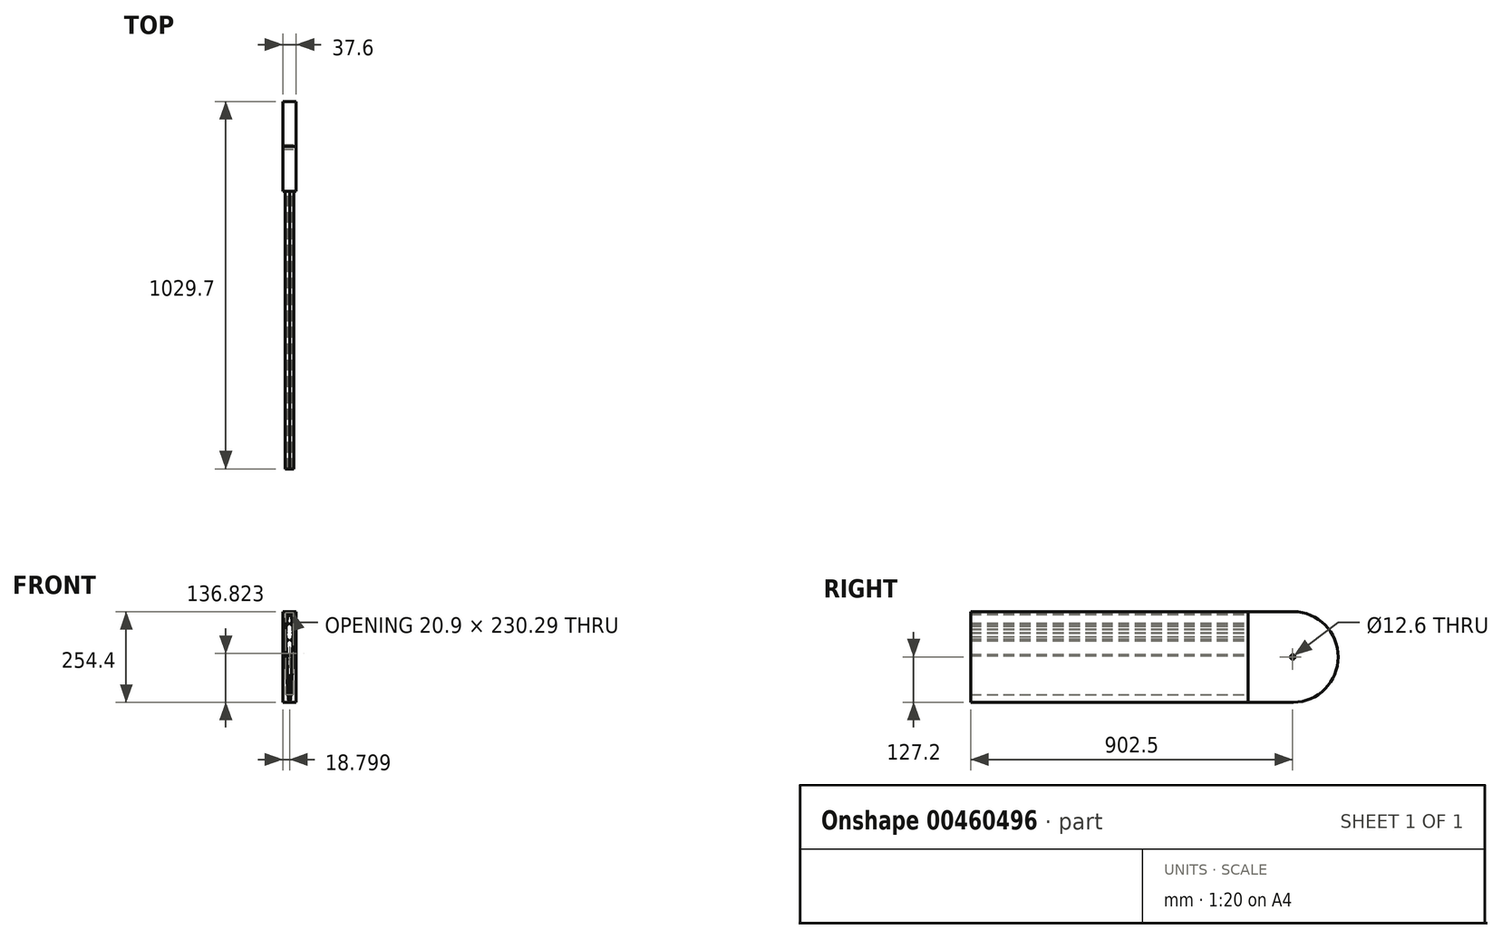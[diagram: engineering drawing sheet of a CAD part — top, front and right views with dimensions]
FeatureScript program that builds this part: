
annotation { "Feature Type Name" : "Feature", "Feature Type Description" : "" }
export const myFeature = defineFeature(function(context is Context, id is Id, definition is map)
    precondition{}
    {
        {
            var Q0;
            Q0=qCreatedBy(makeId("Front.planeOp"),FACE);
            var sketch = newSketch(context, id + "F0", { "sketchPlane" : qUnion([Q0])});
            skLineSegment(sketch, "E0", {"start": v(-26, 84.74) * mm, "end": v(-24.5, 84.74) * mm});
            skArc(sketch, "E1", {"start": v(-26.25, 85) * mm, "mid": v(-26.17, 84.82) * mm, "end": v(-26, 84.74) * mm});
            skFitSpline(sketch, "E2", {"points": [v(-26.25, 85) * mm, v(-26.24, 88.67) * mm, v(-26.08, 98.58) * mm, v(-25.1, 113) * mm, v(-22.87, 125.21) * mm, v(-20.9, 130.42) * mm, v(-19.33, 133.17) * mm, v(-17.9, 134.65) * mm, v(-16.79, 135) * mm, v(-16.24, 135) * mm]});
            skFitSpline(sketch, "E3", {"points": [v(-16.24, 135) * mm, v(-15.7, 135) * mm, v(-14.58, 134.65) * mm, v(-13.16, 133.17) * mm, v(-11.58, 130.42) * mm, v(-9.61, 125.21) * mm, v(-7.38, 113) * mm, v(-6.4, 98.58) * mm, v(-6.24, 88.67) * mm, v(-6.24, 85) * mm]});
            skArc(sketch, "E4", {"start": v(-6.49, 84.74) * mm, "mid": v(-6.3, 84.82) * mm, "end": v(-6.24, 85) * mm});
            skLineSegment(sketch, "E5", {"start": v(-7.99, 84.74) * mm, "end": v(-6.49, 84.74) * mm});
            skArc(sketch, "E6", {"start": v(-7.99, 84.74) * mm, "mid": v(-8.16, 84.67) * mm, "end": v(-8.24, 84.5) * mm});
            skLineSegment(sketch, "E7", {"start": v(-8.24, 84.5) * mm, "end": v(-8.24, 75) * mm});
            skArc(sketch, "E8", {"start": v(-10.24, 88.79) * mm, "mid": v(-10.27, 88.98) * mm, "end": v(-10.38, 89.14) * mm});
            skLineSegment(sketch, "E9", {"start": v(-11.41, 90.17) * mm, "end": v(-10.38, 89.14) * mm});
            skArc(sketch, "E10", {"start": v(-11.44, 90.85) * mm, "mid": v(-11.56, 90.5) * mm, "end": v(-11.41, 90.17) * mm});
            skArc(sketch, "E11", {"start": v(-11.44, 90.85) * mm, "mid": v(-9.9, 95) * mm, "end": v(-11.44, 99.15) * mm});
            skArc(sketch, "E12", {"start": v(-11.41, 99.83) * mm, "mid": v(-11.56, 99.5) * mm, "end": v(-11.44, 99.15) * mm});
            skLineSegment(sketch, "E13", {"start": v(-11.41, 99.83) * mm, "end": v(-9.68, 101.56) * mm});
            skArc(sketch, "E14", {"start": v(-9.68, 101.56) * mm, "mid": v(-9, 102.63) * mm, "end": v(-8.81, 103.89) * mm});
            skFitSpline(sketch, "E15", {"points": [v(-8.81, 103.89) * mm, v(-8.97, 106.15) * mm, v(-9.72, 114.71) * mm, v(-11.32, 123.38) * mm, v(-12.63, 127.4) * mm, v(-12.98, 128.32) * mm]});
            skArc(sketch, "E16", {"start": v(-12.98, 128.32) * mm, "mid": v(-13.34, 128.63) * mm, "end": v(-13.8, 128.5) * mm});
            skArc(sketch, "E17", {"start": v(-14.5, 127.97) * mm, "mid": v(-14.13, 128.21) * mm, "end": v(-13.8, 128.5) * mm});
            skArc(sketch, "E18", {"start": v(-15.24, 128.4) * mm, "mid": v(-15, 127.97) * mm, "end": v(-14.5, 127.97) * mm});
            skLineSegment(sketch, "E19", {"start": v(-15.24, 129) * mm, "end": v(-15.24, 128.4) * mm});
            skArc(sketch, "E20", {"start": v(-15.04, 129.4) * mm, "mid": v(-15.19, 129.22) * mm, "end": v(-15.24, 129) * mm});
            skArc(sketch, "E21", {"start": v(-15.04, 129.4) * mm, "mid": v(-16.24, 133) * mm, "end": v(-17.44, 129.4) * mm});
            skArc(sketch, "E22", {"start": v(-17.24, 129) * mm, "mid": v(-17.3, 129.22) * mm, "end": v(-17.44, 129.4) * mm});
            skLineSegment(sketch, "E23", {"start": v(-17.24, 128.4) * mm, "end": v(-17.24, 129) * mm});
            skArc(sketch, "E24", {"start": v(-18, 127.97) * mm, "mid": v(-17.5, 127.97) * mm, "end": v(-17.24, 128.4) * mm});
            skArc(sketch, "E25", {"start": v(-18.69, 128.5) * mm, "mid": v(-18.36, 128.21) * mm, "end": v(-18, 127.97) * mm});
            skArc(sketch, "E26", {"start": v(-18.69, 128.5) * mm, "mid": v(-19.15, 128.63) * mm, "end": v(-19.5, 128.32) * mm});
            skFitSpline(sketch, "E27", {"points": [v(-19.5, 128.32) * mm, v(-19.86, 127.4) * mm, v(-21.16, 123.38) * mm, v(-22.76, 114.71) * mm, v(-23.52, 106.15) * mm, v(-23.67, 103.89) * mm]});
            skArc(sketch, "E28", {"start": v(-23.67, 103.89) * mm, "mid": v(-23.49, 102.63) * mm, "end": v(-22.8, 101.56) * mm});
            skLineSegment(sketch, "E29", {"start": v(-22.8, 101.56) * mm, "end": v(-21.07, 99.83) * mm});
            skArc(sketch, "E30", {"start": v(-21.05, 99.15) * mm, "mid": v(-20.93, 99.5) * mm, "end": v(-21.07, 99.83) * mm});
            skArc(sketch, "E31", {"start": v(-21.05, 99.15) * mm, "mid": v(-22.6, 95) * mm, "end": v(-21.05, 90.85) * mm});
            skArc(sketch, "E32", {"start": v(-21.07, 90.17) * mm, "mid": v(-20.93, 90.5) * mm, "end": v(-21.05, 90.85) * mm});
            skLineSegment(sketch, "E33", {"start": v(-22.1, 89.14) * mm, "end": v(-21.07, 90.17) * mm});
            skArc(sketch, "E34", {"start": v(-22.1, 89.14) * mm, "mid": v(-22.2, 88.98) * mm, "end": v(-22.25, 88.79) * mm});
            skLineSegment(sketch, "E35", {"start": v(-24.25, 75) * mm, "end": v(-24.25, 84.5) * mm});
            skArc(sketch, "E36", {"start": v(-24.25, 84.5) * mm, "mid": v(-24.32, 84.67) * mm, "end": v(-24.5, 84.74) * mm});
            skLineSegment(sketch, "E37", {"start": v(-8.24, 75) * mm, "end": v(-10.24, 75) * mm});
            skLineSegment(sketch, "E38", {"start": v(-22.25, 88.79) * mm, "end": v(-22.25, 75) * mm});
            skLineSegment(sketch, "E39", {"start": v(-22.25, 75) * mm, "end": v(-24.25, 75) * mm});
            skLineSegment(sketch, "E40", {"start": v(-10.24, 75) * mm, "end": v(-10.24, 88.79) * mm});
            skArc(sketch, "E41", {"start": v(1.9, 35) * mm, "mid": v(5.19, -30.83) * mm, "end": v(9.73, -96.58) * mm});
            skFitSpline(sketch, "E42", {"points": [v(1.9, 35) * mm, v(1.67, 41.44) * mm, v(1.23, 54.34) * mm, v(1.24, 72.62) * mm, v(1.85, 89.82) * mm, v(2.95, 103.2) * mm, v(4.43, 113.85) * mm, v(5.71, 120.45) * mm, v(7.11, 125.63) * mm, v(8.23, 128.8) * mm, v(9.37, 131.23) * mm, v(10.3, 132.77) * mm, v(11.33, 133.95) * mm, v(12.42, 134.8) * mm, v(13.31, 134.93) * mm, v(13.76, 135) * mm]});
            skFitSpline(sketch, "E43", {"points": [v(25.63, 35) * mm, v(25.85, 41.44) * mm, v(26.29, 54.34) * mm, v(26.28, 72.62) * mm, v(25.66, 89.82) * mm, v(24.57, 103.2) * mm, v(23.09, 113.85) * mm, v(21.8, 120.45) * mm, v(20.4, 125.63) * mm, v(19.3, 128.8) * mm, v(18.15, 131.23) * mm, v(17.2, 132.77) * mm, v(16.18, 133.95) * mm, v(15.1, 134.8) * mm, v(14.2, 134.93) * mm, v(13.76, 135) * mm]});
            skArc(sketch, "E44", {"start": v(17.78, -96.58) * mm, "mid": v(22.33, -30.83) * mm, "end": v(25.63, 35) * mm});
            skLineSegment(sketch, "E45", {"start": v(14.84, -134) * mm, "end": v(17.78, -96.58) * mm});
            skLineSegment(sketch, "E46", {"start": v(12.68, -134) * mm, "end": v(9.73, -96.58) * mm});
            skArc(sketch, "E47", {"start": v(11.9, 127.93) * mm, "mid": v(12.51, 128.6) * mm, "end": v(12.32, 129.5) * mm});
            skArc(sketch, "E48", {"start": v(11.9, 127.93) * mm, "mid": v(11.17, 127.47) * mm, "end": v(10.7, 126.74) * mm});
            skFitSpline(sketch, "E49", {"points": [v(6.52, 106.91) * mm, v(6.59, 107.43) * mm, v(7.07, 111.18) * mm, v(8.03, 116.97) * mm, v(9.45, 123.07) * mm, v(10.41, 125.9) * mm, v(10.7, 126.74) * mm]});
            skArc(sketch, "E50", {"start": v(6.52, 106.91) * mm, "mid": v(6.84, 105.55) * mm, "end": v(7.98, 104.73) * mm});
            skArc(sketch, "E51", {"start": v(9.43, 103.98) * mm, "mid": v(8.75, 104.44) * mm, "end": v(7.98, 104.73) * mm});
            skArc(sketch, "E52", {"start": v(8.16, 102.44) * mm, "mid": v(9.56, 102.57) * mm, "end": v(9.43, 103.98) * mm});
            skArc(sketch, "E53", {"start": v(8.16, 102.44) * mm, "mid": v(5.1, 101) * mm, "end": v(8.16, 99.56) * mm});
            skArc(sketch, "E54", {"start": v(9.43, 98.02) * mm, "mid": v(9.56, 99.43) * mm, "end": v(8.16, 99.56) * mm});
            skArc(sketch, "E55", {"start": v(7.22, 97.14) * mm, "mid": v(8.4, 97.4) * mm, "end": v(9.43, 98.02) * mm});
            skArc(sketch, "E56", {"start": v(7.22, 97.14) * mm, "mid": v(5.94, 96.56) * mm, "end": v(5.36, 95.3) * mm});
            skLineSegment(sketch, "E57", {"start": v(5.28, 94.32) * mm, "end": v(5.36, 95.3) * mm});
            skArc(sketch, "E58", {"start": v(5.28, 94.32) * mm, "mid": v(4.02, 90.49) * mm, "end": v(4.8, 86.54) * mm});
            skLineSegment(sketch, "E59", {"start": v(4.72, 84.84) * mm, "end": v(4.8, 86.54) * mm});
            skArc(sketch, "E60", {"start": v(4.72, 84.84) * mm, "mid": v(3.54, 80.36) * mm, "end": v(4.4, 75.81) * mm});
            skLineSegment(sketch, "E61", {"start": v(4.4, 75.18) * mm, "end": v(4.4, 75.81) * mm});
            skArc(sketch, "E62", {"start": v(4.4, 75.18) * mm, "mid": v(3.3, 70.2) * mm, "end": v(4.27, 65.18) * mm});
            skLineSegment(sketch, "E63", {"start": v(4.31, 56.5) * mm, "end": v(4.27, 65.18) * mm});
            skArc(sketch, "E64", {"start": v(4.31, 56.5) * mm, "mid": v(5.37, 53.13) * mm, "end": v(6.65, 56.42) * mm});
            skArc(sketch, "E65", {"start": v(7.96, 57.93) * mm, "mid": v(6.55, 57.83) * mm, "end": v(6.65, 56.42) * mm});
            skArc(sketch, "E66", {"start": v(6.1, 51.19) * mm, "mid": v(9.16, 53.97) * mm, "end": v(7.96, 57.93) * mm});
            skArc(sketch, "E67", {"start": v(6.1, 51.19) * mm, "mid": v(4.9, 50.49) * mm, "end": v(4.44, 49.17) * mm});
            skLineSegment(sketch, "E68", {"start": v(4.89, 35.12) * mm, "end": v(4.44, 49.17) * mm});
            skArc(sketch, "E69", {"start": v(4.89, 35.12) * mm, "mid": v(5.23, 26.93) * mm, "end": v(5.6, 18.75) * mm});
            skArc(sketch, "E70", {"start": v(5.6, 18.75) * mm, "mid": v(6.13, 17.47) * mm, "end": v(7.37, 16.85) * mm});
            skArc(sketch, "E71", {"start": v(9.43, 15.98) * mm, "mid": v(8.46, 16.57) * mm, "end": v(7.37, 16.85) * mm});
            skArc(sketch, "E72", {"start": v(8.15, 14.44) * mm, "mid": v(9.56, 14.57) * mm, "end": v(9.43, 15.98) * mm});
            skArc(sketch, "E73", {"start": v(8.15, 14.44) * mm, "mid": v(5.09, 13) * mm, "end": v(8.15, 11.56) * mm});
            skArc(sketch, "E74", {"start": v(9.43, 10.02) * mm, "mid": v(9.56, 11.43) * mm, "end": v(8.15, 11.56) * mm});
            skArc(sketch, "E75", {"start": v(7.73, 9.2) * mm, "mid": v(8.63, 9.5) * mm, "end": v(9.43, 10.02) * mm});
            skArc(sketch, "E76", {"start": v(7.73, 9.2) * mm, "mid": v(6.55, 8.48) * mm, "end": v(6.14, 7.15) * mm});
            skArc(sketch, "E77", {"start": v(6.14, 7.15) * mm, "mid": v(9.04, -44.62) * mm, "end": v(12.73, -96.34) * mm});
            skLineSegment(sketch, "E78", {"start": v(12.76, -96.8) * mm, "end": v(12.73, -96.34) * mm});
            skArc(sketch, "E79", {"start": v(12.76, -96.8) * mm, "mid": v(13.76, -97.72) * mm, "end": v(14.76, -96.8) * mm});
            skLineSegment(sketch, "E80", {"start": v(14.76, -96.8) * mm, "end": v(14.8, -96.34) * mm});
            skArc(sketch, "E81", {"start": v(14.8, -96.34) * mm, "mid": v(18.47, -44.62) * mm, "end": v(21.38, 7.15) * mm});
            skArc(sketch, "E82", {"start": v(21.38, 7.15) * mm, "mid": v(20.96, 8.48) * mm, "end": v(19.78, 9.2) * mm});
            skArc(sketch, "E83", {"start": v(18.1, 10.02) * mm, "mid": v(18.89, 9.5) * mm, "end": v(19.78, 9.2) * mm});
            skArc(sketch, "E84", {"start": v(19.37, 11.56) * mm, "mid": v(17.96, 11.43) * mm, "end": v(18.1, 10.02) * mm});
            skArc(sketch, "E85", {"start": v(19.37, 11.56) * mm, "mid": v(22.43, 13) * mm, "end": v(19.37, 14.44) * mm});
            skArc(sketch, "E86", {"start": v(20.14, 16.85) * mm, "mid": v(19.05, 16.57) * mm, "end": v(18.1, 15.98) * mm});
            skArc(sketch, "E87", {"start": v(20.14, 16.85) * mm, "mid": v(21.39, 17.47) * mm, "end": v(21.93, 18.75) * mm});
            skArc(sketch, "E88", {"start": v(21.93, 18.75) * mm, "mid": v(22.29, 26.93) * mm, "end": v(22.63, 35.12) * mm});
            skLineSegment(sketch, "E89", {"start": v(22.63, 35.12) * mm, "end": v(23.08, 49.17) * mm});
            skArc(sketch, "E90", {"start": v(23.08, 49.17) * mm, "mid": v(22.62, 50.49) * mm, "end": v(21.42, 51.19) * mm});
            skArc(sketch, "E91", {"start": v(19.56, 57.93) * mm, "mid": v(18.35, 53.97) * mm, "end": v(21.42, 51.19) * mm});
            skArc(sketch, "E92", {"start": v(20.87, 56.42) * mm, "mid": v(20.97, 57.83) * mm, "end": v(19.56, 57.93) * mm});
            skArc(sketch, "E93", {"start": v(20.87, 56.42) * mm, "mid": v(22.15, 53.13) * mm, "end": v(23.2, 56.5) * mm});
            skLineSegment(sketch, "E94", {"start": v(23.2, 56.5) * mm, "end": v(23.25, 65.18) * mm});
            skArc(sketch, "E95", {"start": v(23.25, 65.18) * mm, "mid": v(24.2, 70.2) * mm, "end": v(23.12, 75.18) * mm});
            skArc(sketch, "E96", {"start": v(23.1, 75.81) * mm, "mid": v(23.98, 80.36) * mm, "end": v(22.8, 84.84) * mm});
            skLineSegment(sketch, "E97", {"start": v(22.8, 84.84) * mm, "end": v(22.71, 86.54) * mm});
            skArc(sketch, "E98", {"start": v(22.71, 86.54) * mm, "mid": v(23.5, 90.49) * mm, "end": v(22.23, 94.32) * mm});
            skLineSegment(sketch, "E99", {"start": v(22.23, 94.32) * mm, "end": v(22.16, 95.3) * mm});
            skArc(sketch, "E100", {"start": v(22.16, 95.3) * mm, "mid": v(21.57, 96.56) * mm, "end": v(20.3, 97.14) * mm});
            skArc(sketch, "E101", {"start": v(18.09, 98.02) * mm, "mid": v(19.12, 97.4) * mm, "end": v(20.3, 97.14) * mm});
            skArc(sketch, "E102", {"start": v(19.36, 99.56) * mm, "mid": v(17.95, 99.43) * mm, "end": v(18.09, 98.02) * mm});
            skArc(sketch, "E103", {"start": v(19.36, 99.56) * mm, "mid": v(22.42, 101) * mm, "end": v(19.36, 102.44) * mm});
            skArc(sketch, "E104", {"start": v(18.09, 103.98) * mm, "mid": v(17.95, 102.57) * mm, "end": v(19.36, 102.44) * mm});
            skArc(sketch, "E105", {"start": v(19.54, 104.73) * mm, "mid": v(18.77, 104.44) * mm, "end": v(18.09, 103.98) * mm});
            skArc(sketch, "E106", {"start": v(19.54, 104.73) * mm, "mid": v(20.67, 105.55) * mm, "end": v(21, 106.91) * mm});
            skFitSpline(sketch, "E107", {"points": [v(21, 106.91) * mm, v(20.93, 107.43) * mm, v(20.44, 111.18) * mm, v(19.49, 116.97) * mm, v(18.07, 123.07) * mm, v(17.1, 125.9) * mm, v(16.81, 126.74) * mm]});
            skArc(sketch, "E108", {"start": v(16.81, 126.74) * mm, "mid": v(16.35, 127.47) * mm, "end": v(15.62, 127.93) * mm});
            skArc(sketch, "E109", {"start": v(15.2, 129.5) * mm, "mid": v(15, 128.6) * mm, "end": v(15.62, 127.93) * mm});
            skArc(sketch, "E110", {"start": v(15.2, 129.5) * mm, "mid": v(13.76, 132.57) * mm, "end": v(12.32, 129.5) * mm});
            skArc(sketch, "E111", {"start": v(18.1, 15.98) * mm, "mid": v(17.96, 14.57) * mm, "end": v(19.37, 14.44) * mm});
            skArc(sketch, "E112", {"start": v(12.68, -134) * mm, "mid": v(13.76, -135) * mm, "end": v(14.84, -134) * mm});
            skLineSegment(sketch, "E113", {"start": v(23.12, 75.18) * mm, "end": v(23.1, 75.81) * mm});
            skSolve(sketch);
        }
        {
            var Q0;
            Q0=makeQuery(id+"F0.imprint","IMPRINT",FACE,{"disambiguationData":[TD([[makeQuery(id+"F0.imprint","IMPRINT",EDGE,{"derivedFrom":sQuery(id+"F0.wireOp",EDGE,"E41")}),1.0]])]});
            extrude(context, id + "F1", {"entities" : qUnion([Q0]), "offsetDistance" : 25 * mm, "depth" : 778 * mm});
        }
        {
            var Q0;
            Q0=qCreatedBy(makeId("Front.planeOp"),FACE);
            var sketch = newSketch(context, id + "F2", { "sketchPlane" : qUnion([Q0])});
            skArc(sketch, "E114.0", {"start": v(15.2, 129.5) * mm, "mid": v(13.76, 132.57) * mm, "end": v(12.32, 129.5) * mm, "construction": true});
            skLineSegment(sketch, "E115.bottom", {"start": v(32.56, 135) * mm, "end": v(-5.04, 135) * mm});
            skLineSegment(sketch, "E115.top", {"start": v(32.56, -119.4) * mm, "end": v(-5.04, -119.4) * mm});
            skLineSegment(sketch, "E115.left", {"start": v(32.56, 135) * mm, "end": v(32.56, -119.4) * mm});
            skLineSegment(sketch, "E115.right", {"start": v(-5.04, 135) * mm, "end": v(-5.04, -119.4) * mm});
            skSolve(sketch);
        }
        {
            var Q0;
            Q0 = qSketchRegion(id + "F2", true);
            extrude(context, id + "F3", {"entities" : qUnion([Q0]), "oppositeDirection" : true, "depth" : 251.7 * mm, "offsetDistance" : 25 * mm});
        }
        {
            var Q0;
            Q0=makeQuery(id+"F3.opExtrude","SWEPT_FACE",FACE,{"disambiguationData":[OSD([sQuery(id+"F2.wireOp",EDGE,"E115.left")])]});
            var sketch = newSketch(context, id + "F4", { "sketchPlane" : qUnion([Q0])});
            skCircle(sketch, "E116", {"center": v(124.5, 7.8) * mm, "radius": 127.2 * mm});
            skPoint(sketch, "E117.firstSnap0", {"position": v(125.85, 135) * mm});
            skLineSegment(sketch, "E117.bottom", {"start": v(125.85, 135) * mm, "end": v(311.02, 135) * mm});
            skLineSegment(sketch, "E117.top", {"start": v(125.85, -119.4) * mm, "end": v(311.02, -119.4) * mm});
            skLineSegment(sketch, "E117.left", {"start": v(125.85, 135) * mm, "end": v(125.85, -119.4) * mm});
            skLineSegment(sketch, "E117.right", {"start": v(311.02, 135) * mm, "end": v(311.02, -119.4) * mm});
            skCircle(sketch, "E118", {"center": v(124.5, 7.8) * mm, "radius": 6.3 * mm});
            skSolve(sketch);
        }
        {
            var Q0;
            {var subQ0=sQuery(id+"F4.wireOp",EDGE,"E118");var subQ1=sQuery(id+"F4.wireOp",EDGE,"E117.left");var subQ2=makeQuery(id+"F4.imprint","INTERSECT",VERTEX,{"disambiguationData":[OD(0.0)],"derivedFrom":[subQ1,subQ0]});Q0=makeQuery(id+"F4.imprint","IMPRINT",FACE,{"disambiguationData":[TD([[makeQuery(id+"F4.imprint","IMPRINT",EDGE,{"disambiguationData":[TD([[subQ2,-1.0]])],"derivedFrom":subQ1}),-1.0]])]});}
            var Q1;
            {var subQ0=sQuery(id+"F4.wireOp",EDGE,"E118");var subQ1=sQuery(id+"F4.wireOp",EDGE,"E117.left");var subQ2=makeQuery(id+"F4.imprint","INTERSECT",VERTEX,{"disambiguationData":[OD(0.0)],"derivedFrom":[subQ1,subQ0]});Q1=makeQuery(id+"F4.imprint","IMPRINT",FACE,{"disambiguationData":[TD([[makeQuery(id+"F4.imprint","IMPRINT",EDGE,{"disambiguationData":[TD([[subQ2,-1.0]])],"derivedFrom":subQ1}),1.0]])]});}
            var Q2;
            {var subQ0=sQuery(id+"F4.wireOp",EDGE,"E117.bottom");var subQ3=makeQuery(id+"F3.opExtrude","CAP_EDGE",EDGE,{"disambiguationData":[OSD([sQuery(id+"F2.wireOp",EDGE,"E115.left")])],"isStart":false});var subQ5=makeQuery(id+"F4.imprint","INTERSECT",VERTEX,{"derivedFrom":[subQ3,subQ0]});Q2=makeQuery(id+"F4.imprint","IMPRINT",FACE,{"disambiguationData":[TD([[makeQuery(id+"F4.imprint","IMPRINT",EDGE,{"disambiguationData":[TD([[subQ5,-1.0]])],"derivedFrom":subQ3}),-1.0]])]});}
            var Q3;
            {var subQ0=sQuery(id+"F4.wireOp",EDGE,"E117.left");var subQ1=sQuery(id+"F4.wireOp",EDGE,"E116");var subQ2=makeQuery(id+"F4.imprint","INTERSECT",VERTEX,{"derivedFrom":[subQ1,subQ0]});Q3=makeQuery(id+"F4.imprint","IMPRINT",FACE,{"disambiguationData":[TD([[makeQuery(id+"F4.imprint","IMPRINT",EDGE,{"disambiguationData":[TD([[subQ2,-1.0]])],"derivedFrom":subQ1}),-1.0]])]});}
            extrude(context, id + "F5", {"entities" : qUnion([Q0, Q1, Q2, Q3]), "operationType" : NewBodyOperationType.REMOVE, "endBound" : BoundingType.THROUGH_ALL, "oppositeDirection" : true, "depth" : 25 * mm, "offsetDistance" : 25 * mm});
        }
        {
            var Q0;
            Q0=makeQuery(id+"F3.opExtrude","SWEPT_FACE",FACE,{"disambiguationData":[OSD([sQuery(id+"F2.wireOp",EDGE,"E115.right")])]});
            var sketch = newSketch(context, id + "F6", { "sketchPlane" : qUnion([Q0])});
            skCircle(sketch, "E119.cCircle", {"center": v(-124.5, 7.8) * mm, "radius": 127.2 * mm, "construction": true});
            skLineSegment(sketch, "E119.0", {"start": v(-251.7, -17.5) * mm, "end": v(-251.7, 33.1) * mm});
            skLineSegment(sketch, "E119.1", {"start": v(-251.7, 33.1) * mm, "end": v(-232.33, 79.85) * mm});
            skLineSegment(sketch, "E119.2", {"start": v(-232.33, 79.85) * mm, "end": v(-196.55, 115.63) * mm});
            skLineSegment(sketch, "E119.3", {"start": v(-196.55, 115.63) * mm, "end": v(-149.8, 135) * mm});
            skLineSegment(sketch, "E119.4", {"start": v(-149.8, 135) * mm, "end": v(-99.2, 135) * mm});
            skLineSegment(sketch, "E119.5", {"start": v(-99.2, 135) * mm, "end": v(-52.45, 115.63) * mm});
            skLineSegment(sketch, "E119.6", {"start": v(-52.45, 115.63) * mm, "end": v(-16.67, 79.85) * mm});
            skLineSegment(sketch, "E119.7", {"start": v(-16.67, 79.85) * mm, "end": v(2.7, 33.1) * mm});
            skLineSegment(sketch, "E119.8", {"start": v(2.7, 33.1) * mm, "end": v(2.7, -17.5) * mm});
            skLineSegment(sketch, "E119.9", {"start": v(2.7, -17.5) * mm, "end": v(-16.67, -64.25) * mm});
            skLineSegment(sketch, "E119.10", {"start": v(-16.67, -64.25) * mm, "end": v(-52.45, -100.03) * mm});
            skLineSegment(sketch, "E119.11", {"start": v(-52.45, -100.03) * mm, "end": v(-99.2, -119.4) * mm});
            skLineSegment(sketch, "E119.12", {"start": v(-99.2, -119.4) * mm, "end": v(-149.8, -119.4) * mm});
            skLineSegment(sketch, "E119.13", {"start": v(-149.8, -119.4) * mm, "end": v(-196.55, -100.03) * mm});
            skLineSegment(sketch, "E119.14", {"start": v(-196.55, -100.03) * mm, "end": v(-232.33, -64.25) * mm});
            skLineSegment(sketch, "E119.15", {"start": v(-232.33, -64.25) * mm, "end": v(-251.7, -17.5) * mm});
            skPoint(sketch, "E119.0.midPoint", {"position": v(-251.7, 7.8) * mm});
            skSolve(sketch);
        }
        {
            var Q0;
            Q0=makeQuery(id+"F1.opExtrude","CAP_FACE",FACE,{"disambiguationData":[OSD([sQuery(id+"F0.wireOp",EDGE,"E41"),sQuery(id+"F0.wireOp",EDGE,"E42"),sQuery(id+"F0.wireOp",EDGE,"E43"),sQuery(id+"F0.wireOp",EDGE,"E44"),sQuery(id+"F0.wireOp",EDGE,"E45"),sQuery(id+"F0.wireOp",EDGE,"E46"),sQuery(id+"F0.wireOp",EDGE,"E47"),sQuery(id+"F0.wireOp",EDGE,"E48"),sQuery(id+"F0.wireOp",EDGE,"E49"),sQuery(id+"F0.wireOp",EDGE,"E50"),sQuery(id+"F0.wireOp",EDGE,"E51"),sQuery(id+"F0.wireOp",EDGE,"E52"),sQuery(id+"F0.wireOp",EDGE,"E53"),sQuery(id+"F0.wireOp",EDGE,"E54"),sQuery(id+"F0.wireOp",EDGE,"E55"),sQuery(id+"F0.wireOp",EDGE,"E56"),sQuery(id+"F0.wireOp",EDGE,"E57"),sQuery(id+"F0.wireOp",EDGE,"E58"),sQuery(id+"F0.wireOp",EDGE,"E59"),sQuery(id+"F0.wireOp",EDGE,"E60"),sQuery(id+"F0.wireOp",EDGE,"E61"),sQuery(id+"F0.wireOp",EDGE,"E62"),sQuery(id+"F0.wireOp",EDGE,"E63"),sQuery(id+"F0.wireOp",EDGE,"E64"),sQuery(id+"F0.wireOp",EDGE,"E65"),sQuery(id+"F0.wireOp",EDGE,"E66"),sQuery(id+"F0.wireOp",EDGE,"E67"),sQuery(id+"F0.wireOp",EDGE,"E68"),sQuery(id+"F0.wireOp",EDGE,"E69"),sQuery(id+"F0.wireOp",EDGE,"E70"),sQuery(id+"F0.wireOp",EDGE,"E71"),sQuery(id+"F0.wireOp",EDGE,"E72"),sQuery(id+"F0.wireOp",EDGE,"E73"),sQuery(id+"F0.wireOp",EDGE,"E74"),sQuery(id+"F0.wireOp",EDGE,"E75"),sQuery(id+"F0.wireOp",EDGE,"E76"),sQuery(id+"F0.wireOp",EDGE,"E77"),sQuery(id+"F0.wireOp",EDGE,"E78"),sQuery(id+"F0.wireOp",EDGE,"E79"),sQuery(id+"F0.wireOp",EDGE,"E80"),sQuery(id+"F0.wireOp",EDGE,"E81"),sQuery(id+"F0.wireOp",EDGE,"E82"),sQuery(id+"F0.wireOp",EDGE,"E83"),sQuery(id+"F0.wireOp",EDGE,"E84"),sQuery(id+"F0.wireOp",EDGE,"E85"),sQuery(id+"F0.wireOp",EDGE,"E86"),sQuery(id+"F0.wireOp",EDGE,"E87"),sQuery(id+"F0.wireOp",EDGE,"E88"),sQuery(id+"F0.wireOp",EDGE,"E89"),sQuery(id+"F0.wireOp",EDGE,"E90"),sQuery(id+"F0.wireOp",EDGE,"E91"),sQuery(id+"F0.wireOp",EDGE,"E92"),sQuery(id+"F0.wireOp",EDGE,"E93"),sQuery(id+"F0.wireOp",EDGE,"E94"),sQuery(id+"F0.wireOp",EDGE,"E95"),sQuery(id+"F0.wireOp",EDGE,"E96"),sQuery(id+"F0.wireOp",EDGE,"E97"),sQuery(id+"F0.wireOp",EDGE,"E98"),sQuery(id+"F0.wireOp",EDGE,"E99"),sQuery(id+"F0.wireOp",EDGE,"E100"),sQuery(id+"F0.wireOp",EDGE,"E101"),sQuery(id+"F0.wireOp",EDGE,"E102"),sQuery(id+"F0.wireOp",EDGE,"E103"),sQuery(id+"F0.wireOp",EDGE,"E104"),sQuery(id+"F0.wireOp",EDGE,"E105"),sQuery(id+"F0.wireOp",EDGE,"E106"),sQuery(id+"F0.wireOp",EDGE,"E107"),sQuery(id+"F0.wireOp",EDGE,"E108"),sQuery(id+"F0.wireOp",EDGE,"E109"),sQuery(id+"F0.wireOp",EDGE,"E110"),sQuery(id+"F0.wireOp",EDGE,"E111"),sQuery(id+"F0.wireOp",EDGE,"E112"),sQuery(id+"F0.wireOp",EDGE,"E113")])],"isStart":true});
            var sketch = newSketch(context, id + "F7", { "sketchPlane" : qUnion([Q0])});
            skLineSegment(sketch, "E120.bottom", {"start": v(-32.56, -119.4) * mm, "end": v(5.04, -119.4) * mm});
            skLineSegment(sketch, "E120.top", {"start": v(-32.56, -139.4) * mm, "end": v(5.04, -139.4) * mm});
            skLineSegment(sketch, "E120.left", {"start": v(-32.56, -119.4) * mm, "end": v(-32.56, -139.4) * mm});
            skLineSegment(sketch, "E120.right", {"start": v(5.04, -119.4) * mm, "end": v(5.04, -139.4) * mm});
            skSolve(sketch);
        }
        {
            var Q0;
            Q0 = qSketchRegion(id + "F7", true);
            extrude(context, id + "F8", {"entities" : qUnion([Q0]), "operationType" : NewBodyOperationType.REMOVE, "endBound" : BoundingType.THROUGH_ALL, "oppositeDirection" : true, "depth" : 25 * mm, "offsetDistance" : 25 * mm});
        }
    });
